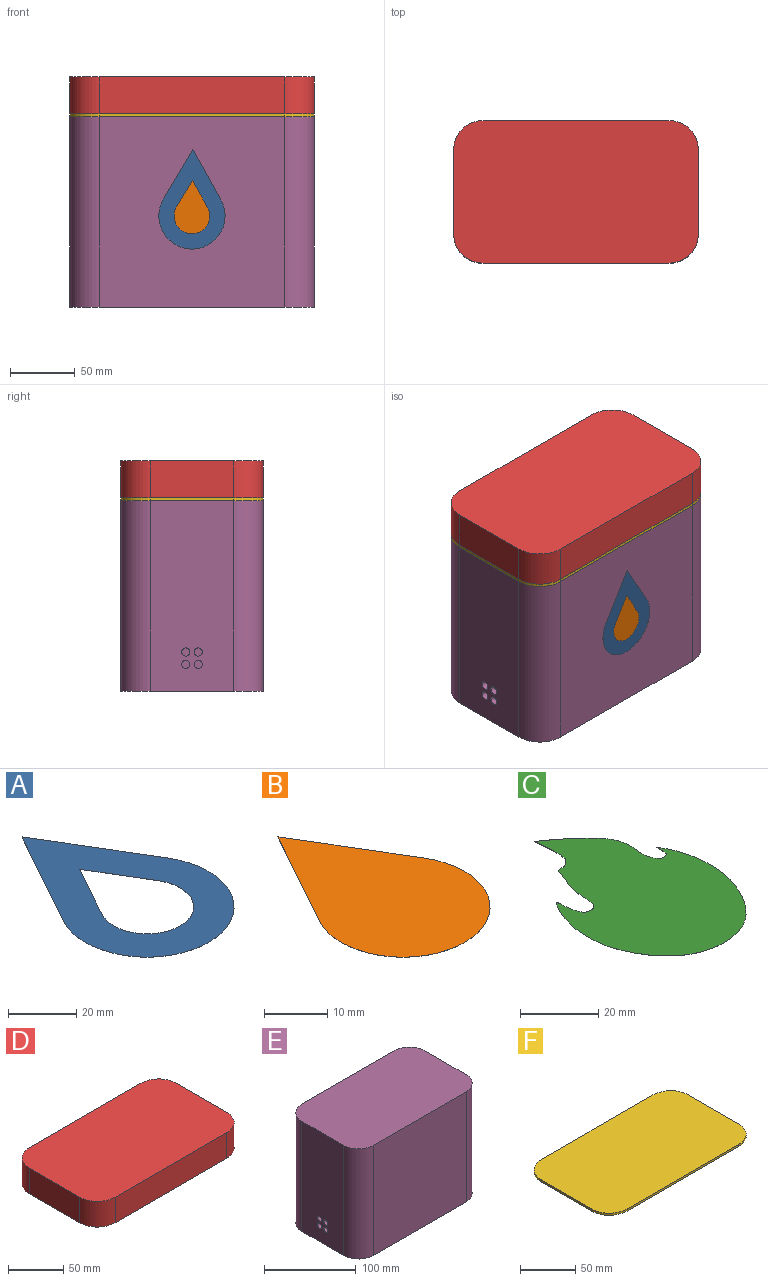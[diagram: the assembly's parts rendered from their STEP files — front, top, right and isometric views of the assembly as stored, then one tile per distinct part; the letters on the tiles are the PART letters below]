
ASSEMBLY  parts=6 mates=5
PART A: 8 faces, bbox 51.2x76.8x0 mm
  f0: plane 38.73x21.58mm, normal (-0.87,0.49,0), area 1mm2, adj f1,f5,f6,f7
  f1: cylinder r=25.6mm len=51.2mm, axis (0,0,-1), area 2.4mm2, adj f0,f5,f6,f7
  f2: cylinder r=13.75mm len=27.49mm, axis (0,0,-1), area 1.3mm2, adj f3,f4,f6,f7
  f3: plane 20.8x11.59mm, normal (0.87,-0.49,0), area 0.5mm2, adj f2,f4,f6,f7
  f4: plane 20.44x12.22mm, normal (-0.86,-0.51,0), area 0.5mm2, adj f2,f3,f6,f7
  f5: plane 38.06x22.75mm, normal (0.86,0.51,0), area 1mm2, adj f0,f1,f6,f7
  f6: plane 76.79x51.2mm, normal (0,0,1), area 1784.6mm2, adj f0,f1,f2,f3,f4,f5
  f7: plane 76.79x51.2mm, normal (0,0,-1), area 1784.6mm2, adj f0,f1,f2,f3,f4,f5
PART B: 5 faces, bbox 27.5x41.2x0 mm
  f0: plane 20.8x11.59mm, normal (-0.87,0.49,0), area 0.5mm2, adj f1,f2,f3,f4
  f1: cylinder r=13.75mm len=27.49mm, axis (0,0,-1), area 1.3mm2, adj f0,f2,f3,f4
  f2: plane 20.44x12.22mm, normal (0.86,0.51,0), area 0.5mm2, adj f0,f1,f3,f4
  f3: plane 41.24x27.49mm, normal (0,0,1), area 723.1mm2, adj f0,f1,f2
  f4: plane 41.24x27.49mm, normal (0,0,-1), area 723.1mm2, adj f0,f1,f2
PART C: 18 faces, bbox 46.8x66x0 mm
  f0: extruded ~4.41x3.19mm, area 0.1mm2, adj f1,f15,f16,f17
  f1: extruded ~6.53x0.61mm, area 0.2mm2, adj f0,f2,f16,f17
  f2: extruded ~4.8x0.61mm, area 0.1mm2, adj f1,f3,f16,f17
  f3: extruded ~2.79x1.98mm, area 0.1mm2, adj f2,f4,f16,f17
  f4: extruded ~1.79x0.03mm, area 0mm2, adj f3,f5,f16,f17
  f5: extruded ~9.2x3.4mm, area 0.2mm2, adj f4,f6,f16,f17
  f6: extruded ~4.67x0.52mm, area 0.1mm2, adj f5,f7,f16,f17
  f7: extruded ~7.45x6.28mm, area 0.4mm2, adj f6,f8,f16,f17
  f8: extruded ~0.95x0.27mm, area 0mm2, adj f7,f9,f16,f17
  f9: extruded ~6.36x3.46mm, area 0.2mm2, adj f8,f10,f16,f17
  f10: extruded ~16.89x1.65mm, area 0.4mm2, adj f9,f11,f16,f17
  f11: extruded ~43.9x41.89mm, area 2.2mm2, adj f10,f12,f16,f17
  f12: extruded ~1.73x0.55mm, area 0mm2, adj f11,f13,f16,f17
  f13: extruded ~1.95x1.84mm, area 0.1mm2, adj f12,f14,f16,f17
  f14: extruded ~17.94x5.65mm, area 0.5mm2, adj f13,f15,f16,f17
  f15: extruded ~6.23x5.28mm, area 0.2mm2, adj f0,f14,f16,f17
  f16: plane 65.98x46.8mm, normal (0,0,1), area 1789.3mm2, adj f0,f1,f2,f3,f4,f5,f6,f7
  f17: plane 65.98x46.8mm, normal (0,0,-1), area 1789.3mm2, adj f0,f1,f2,f3,f4,f5,f6,f7
PART D: 10 faces, bbox 189.1x110.1x28.5 mm
  f0: plane 143.47x28.49mm, normal (0,1,0), area 4087.8mm2, adj f4,f5,f8,f9
  f1: plane 64.54x28.49mm, normal (-1,0,0), area 1839.1mm2, adj f4,f5,f6,f9
  f2: plane 143.47x28.49mm, normal (0,-1,0), area 4087.8mm2, adj f4,f6,f7,f9
  f3: plane 64.54x28.49mm, normal (1,0,0), area 1839.1mm2, adj f4,f7,f8,f9
  f4: plane 189.06x110.13mm, normal (0,0,1), area 20375.2mm2, adj f0,f1,f2,f3,f5,f6,f7,f8
  f5: cylinder r=22.79mm len=28.49mm, axis (0,0,1), area 1020.2mm2, adj f0,f1,f4,f9
  f6: cylinder r=22.79mm len=28.49mm, axis (0,0,-1), area 1020.2mm2, adj f1,f2,f4,f9
  f7: cylinder r=22.79mm len=28.49mm, axis (0,0,1), area 1020.2mm2, adj f2,f3,f4,f9
  f8: cylinder r=22.79mm len=28.49mm, axis (0,0,-1), area 1020.2mm2, adj f0,f3,f4,f9
  f9: plane 189.06x110.13mm, normal (0,0,-1), area 20375.2mm2, adj f0,f1,f2,f3,f5,f6,f7,f8
PART E: 18 faces, bbox 189.1x110.1x147 mm
  f0: plane 189.06x110.13mm, normal (0,0,1), area 20375.2mm2, adj f2,f3,f4,f5,f6,f7,f8,f9
  f1: plane 189.06x110.13mm, normal (0,0,-1), area 20375.2mm2, adj f2,f3,f4,f5,f6,f7,f8,f9
  f2: cylinder r=22.79mm len=147.03mm, axis (0,0,1), area 5264.5mm2, adj f0,f1,f4,f6
  f3: cylinder r=22.79mm len=147.03mm, axis (0,0,-1), area 5264.5mm2, adj f0,f1,f4,f9
  f4: plane 147.03x64.54mm, normal (1,0,0), area 9489.6mm2, adj f0,f1,f2,f3
  f5: cylinder r=22.79mm len=147.03mm, axis (0,0,-1), area 5264.5mm2, adj f0,f1,f6,f8
  f6: plane 147.03x143.47mm, normal (0,-1,0), area 21093.3mm2, adj f0,f1,f2,f5
  f7: cylinder r=22.79mm len=147.03mm, axis (0,0,1), area 5264.5mm2, adj f0,f1,f8,f9
  f8: plane 147.03x64.54mm, normal (-1,0,0), area 9362.9mm2, adj f0,f1,f5,f7,f10,f12,f14,f16
  f9: plane 147.03x143.47mm, normal (0,1,0), area 21093.3mm2, adj f0,f1,f3,f7
  f10: cylinder r=3.17mm len=25.4mm, axis (-1,0,0), area 506.7mm2, adj f8,f11
  f11: plane 6.35x6.35mm, normal (-1,0,0), area 31.7mm2, adj f10
  f12: cylinder r=3.17mm len=25.4mm, axis (-1,0,0), area 506.7mm2, adj f8,f13
  f13: plane 6.35x6.35mm, normal (-1,0,0), area 31.7mm2, adj f12
  f14: cylinder r=3.17mm len=25.4mm, axis (-1,0,0), area 506.7mm2, adj f8,f15
  f15: plane 6.35x6.35mm, normal (-1,0,0), area 31.7mm2, adj f14
  f16: cylinder r=3.17mm len=25.4mm, axis (-1,0,0), area 506.7mm2, adj f8,f17
  f17: plane 6.35x6.35mm, normal (-1,0,0), area 31.7mm2, adj f16
PART F: 10 faces, bbox 189.1x110.1x2.3 mm
  f0: plane 143.47x2.28mm, normal (0,1,0), area 327mm2, adj f1,f7,f8,f9
  f1: cylinder r=22.79mm len=22.8mm, axis (0,0,-1), area 81.6mm2, adj f0,f2,f8,f9
  f2: plane 64.54x2.28mm, normal (-1,0,0), area 147.1mm2, adj f1,f3,f8,f9
  f3: cylinder r=22.79mm len=22.8mm, axis (0,0,-1), area 81.6mm2, adj f2,f4,f8,f9
  f4: plane 143.47x2.28mm, normal (0,-1,0), area 327mm2, adj f3,f5,f8,f9
  f5: cylinder r=22.79mm len=22.8mm, axis (0,0,-1), area 81.6mm2, adj f4,f6,f8,f9
  f6: plane 64.54x2.28mm, normal (1,0,0), area 147.1mm2, adj f5,f7,f8,f9
  f7: cylinder r=22.79mm len=22.8mm, axis (0,0,-1), area 81.6mm2, adj f0,f6,f8,f9
  f8: plane 189.06x110.13mm, normal (0,0,1), area 20375.2mm2, adj f0,f1,f2,f3,f4,f5,f6,f7
  f9: plane 189.06x110.13mm, normal (0,0,-1), area 20375.2mm2, adj f0,f1,f2,f3,f4,f5,f6,f7
PLACE A rot(axis=(0,0.71,0.71),180deg) t=(-113.6,-106.26,-176.26)mm
PLACE B rot(axis=(0,0.71,0.71),180deg) t=(-113.6,-106.26,-176.26)mm
PLACE C rot(axis=(1,0,0),90deg) t=(-114.5,3.93,-158.5)mm
PLACE D t=(-19.02,-106.23,-244.38)mm
PLACE E t=(-19.02,-106.23,-246.66)mm
PLACE F rot(axis=(1,0,0),180deg) t=(-19.02,3.9,78.17)mm
MATE fastened F.f8 <-> E.f0  axis (0,0,-1) through (-113.55,-51.17,-99.63)mm
MATE fastened D.f9 <-> F.f9  axis (0,0,-1) through (-113.55,-51.17,-97.35)mm
MATE fastened A.f6 <-> B.f3  axis (0,1,0) through (-113.18,-106.23,-148.77)mm
MATE fastened B.f3 <-> E.f6  axis (0,1,0) through (-113.55,-106.23,-173.15)mm
MATE fastened C.f16 <-> E.f9  axis (0,-1,0) through (-113.55,3.9,-173.15)mm
